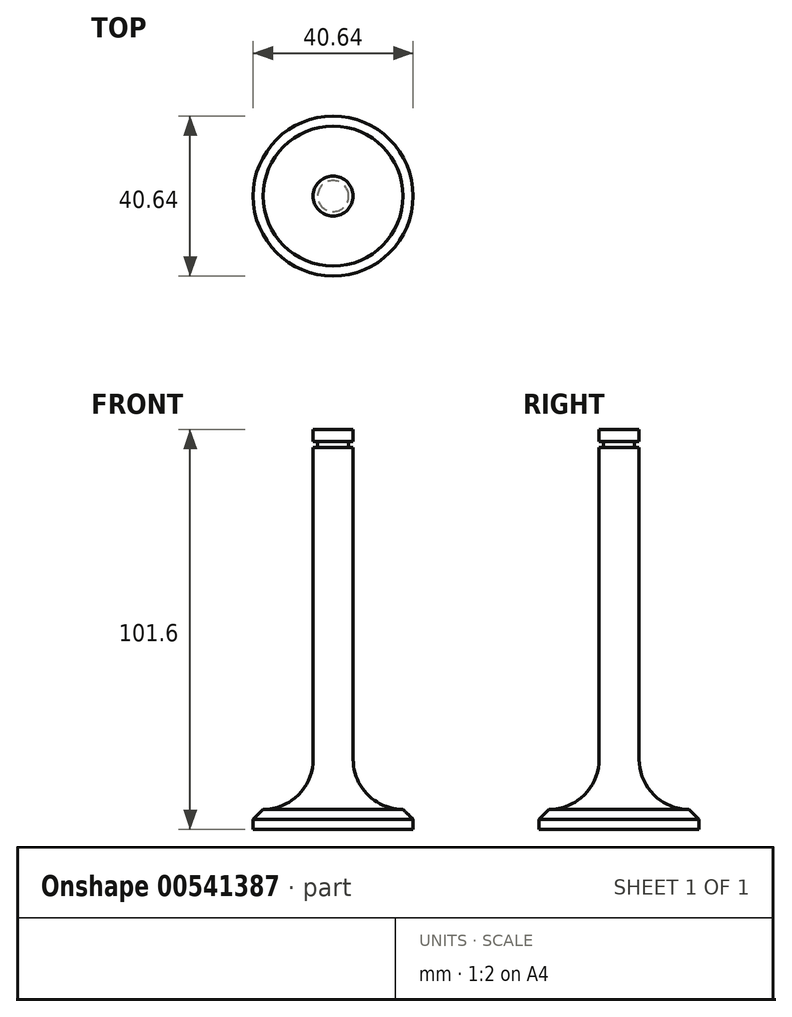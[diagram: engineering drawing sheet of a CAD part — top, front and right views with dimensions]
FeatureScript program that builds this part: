
annotation { "Feature Type Name" : "Feature", "Feature Type Description" : "" }
export const myFeature = defineFeature(function(context is Context, id is Id, definition is map)
    precondition{}
    {
        {
            var Q0;
            Q0=qCreatedBy(makeId("Front.planeOp"),FACE);
            var sketch = newSketch(context, id + "F0", { "sketchPlane" : qUnion([Q0])});
            skLineSegment(sketch, "E0", {"start": v(0, -9.64) * mm, "end": v(-20.32, -9.64) * mm});
            skLineSegment(sketch, "E1", {"start": v(-20.32, -9.64) * mm, "end": v(-20.32, -7.1) * mm});
            skLineSegment(sketch, "E2", {"start": v(-20.32, -7.1) * mm, "end": v(-17.78, -4.56) * mm});
            skLineSegment(sketch, "E3", {"start": v(-17.78, -4.56) * mm, "end": v(-17.78, -4.56) * mm});
            skLineSegment(sketch, "E4", {"start": v(-5.08, 91.96) * mm, "end": v(-5.08, 88.92) * mm});
            skPoint(sketch, "E5.orphan", {"position": v(0, -4.56) * mm});
            skLineSegment(sketch, "E6", {"start": v(-5.08, 91.96) * mm, "end": v(0, 91.96) * mm});
            skLineSegment(sketch, "E7", {"start": v(0, 91.96) * mm, "end": v(0, -10.85) * mm});
            skLineSegment(sketch, "E8", {"start": v(-5.08, 88.92) * mm, "end": v(-3.94, 88.92) * mm});
            skLineSegment(sketch, "E9", {"start": v(-3.94, 88.92) * mm, "end": v(-3.94, 87.37) * mm});
            skLineSegment(sketch, "E10", {"start": v(-3.94, 87.37) * mm, "end": v(-5.08, 87.37) * mm});
            skLineSegment(sketch, "E11.trimOffspring", {"start": v(-5.08, 87.37) * mm, "end": v(-5.08, 8.14) * mm});
            skPoint(sketch, "E12.orphan", {"position": v(0, 88.92) * mm});
            skPoint(sketch, "E13.visualSharp", {"position": v(-5.08, -4.56) * mm});
            skArc(sketch, "E13.filletArc", {"start": v(-17.78, -4.56) * mm, "mid": v(-8.8, -0.84) * mm, "end": v(-5.08, 8.14) * mm});
            skSolve(sketch);
        }
        {
            var Q0;
            {var subQ1=sQuery(id+"F0.wireOp",EDGE,"E0");Q0=makeQuery(id+"F0.imprint","IMPRINT",FACE,{"disambiguationData":[TD([[makeQuery(id+"F0.imprint","IMPRINT",EDGE,{"derivedFrom":subQ1}),-1.0]])]});}
            var Q1;
            Q1=sQuery(id+"F0.wireOp",EDGE,"E7");
            revolve(context, id + "F1", {"entities" : qUnion([Q0]), "axis" : qUnion([Q1]), "revolveType" : RevolveType.FULL});
        }
    });
